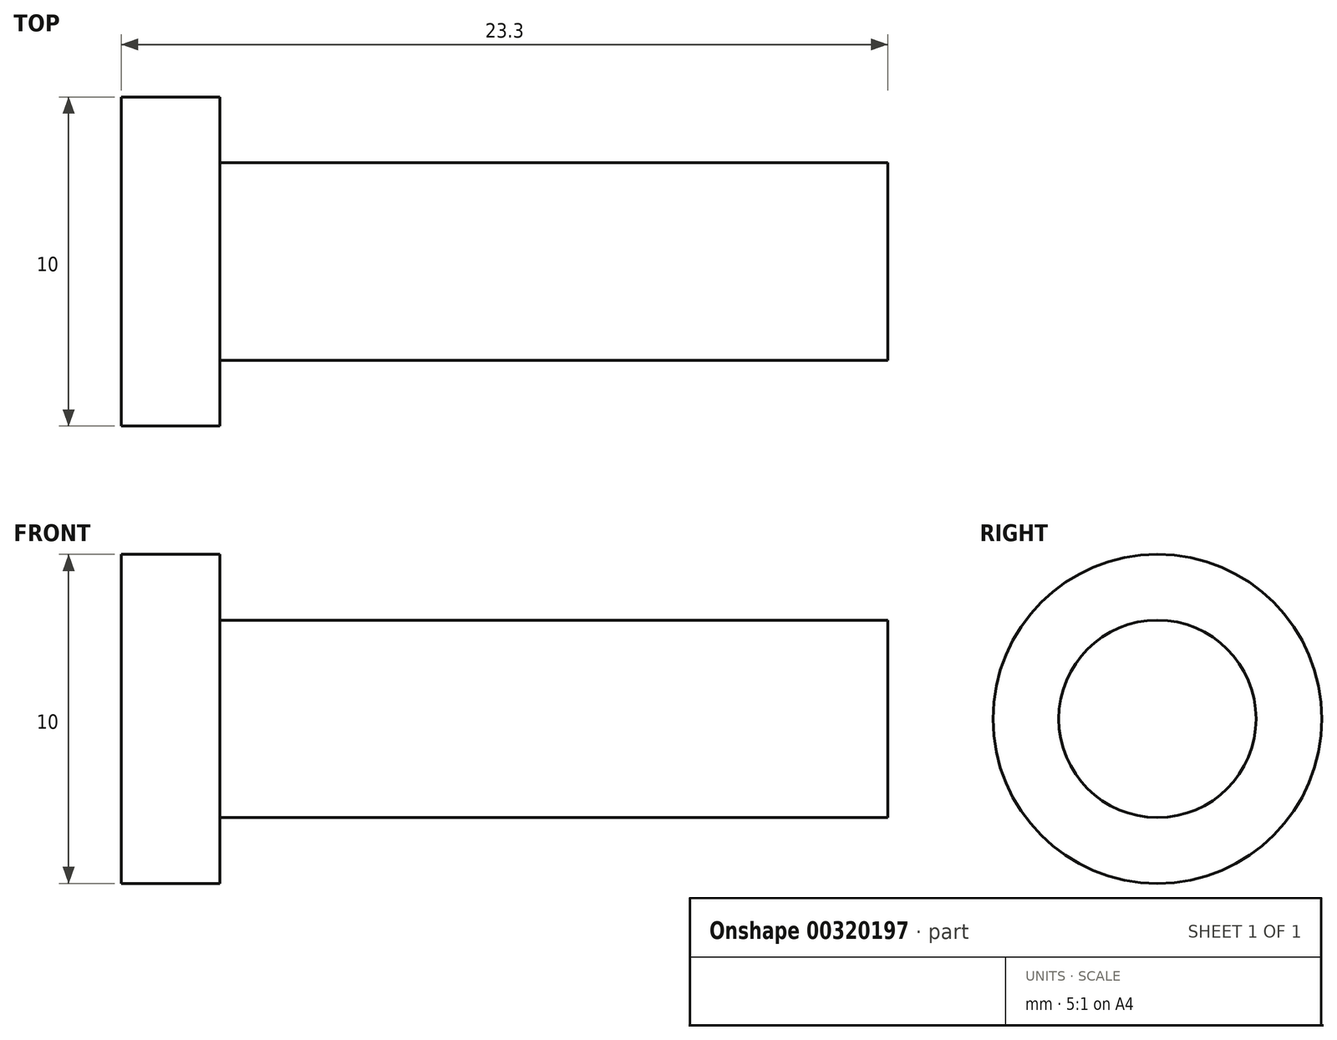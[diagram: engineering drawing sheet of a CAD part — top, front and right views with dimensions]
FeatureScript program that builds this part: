
annotation { "Feature Type Name" : "Feature", "Feature Type Description" : "" }
export const myFeature = defineFeature(function(context is Context, id is Id, definition is map)
    precondition{}
    {
        {
            var Q0;
            Q0=qCreatedBy(makeId("Front.planeOp"),FACE);
            var sketch = newSketch(context, id + "F0", { "sketchPlane" : qUnion([Q0])});
            skLineSegment(sketch, "E0.bottom", {"start": v(-12.79, 3) * mm, "end": v(7.51, 3) * mm});
            skLineSegment(sketch, "E0.top", {"start": v(-12.79, 0) * mm, "end": v(7.51, 0) * mm});
            skLineSegment(sketch, "E0.left", {"start": v(-12.79, 3) * mm, "end": v(-12.79, 0) * mm});
            skLineSegment(sketch, "E0.right", {"start": v(7.51, 3) * mm, "end": v(7.51, 0) * mm});
            skLineSegment(sketch, "E1.bottom", {"start": v(-12.79, 0) * mm, "end": v(-15.79, 0) * mm});
            skLineSegment(sketch, "E1.top", {"start": v(-12.79, 5) * mm, "end": v(-15.79, 5) * mm});
            skLineSegment(sketch, "E1.left", {"start": v(-12.79, 0) * mm, "end": v(-12.79, 5) * mm});
            skLineSegment(sketch, "E1.right", {"start": v(-15.79, 0) * mm, "end": v(-15.79, 5) * mm});
            skSolve(sketch);
        }
        {
            var Q0;
            Q0 = qSketchRegion(id + "F0", true);
            var Q1;
            Q1=sQuery(id+"F0.wireOp",EDGE,"E0.top");
            revolve(context, id + "F1", {"entities" : qUnion([Q0]), "axis" : qUnion([Q1]), "revolveType" : RevolveType.FULL});
        }
    });
